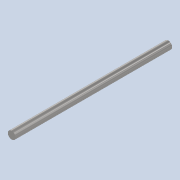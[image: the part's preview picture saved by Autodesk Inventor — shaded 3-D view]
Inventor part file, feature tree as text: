
AUTODESK INVENTOR PART (.ipt)
format: ipt  version: 2020 (Build 240168000, 168)  size: 80,896 bytes
history: native  units: mm
features: extrude x1, sketch x1
ambient origin geometry x8: Origin, YZ Plane, XZ Plane, XY Plane, X Axis, Y Axis, Z Axis, Center Point
bodies: Solid1 (feature_tree)
feature tree (2):
  extrude  "Extrusion1"  Depth=163.0mm TaperAngle=0.0deg
  sketch  "Sketch1"  dims[d0=8.0mm d1=163.0mm d2=0.0mm]
